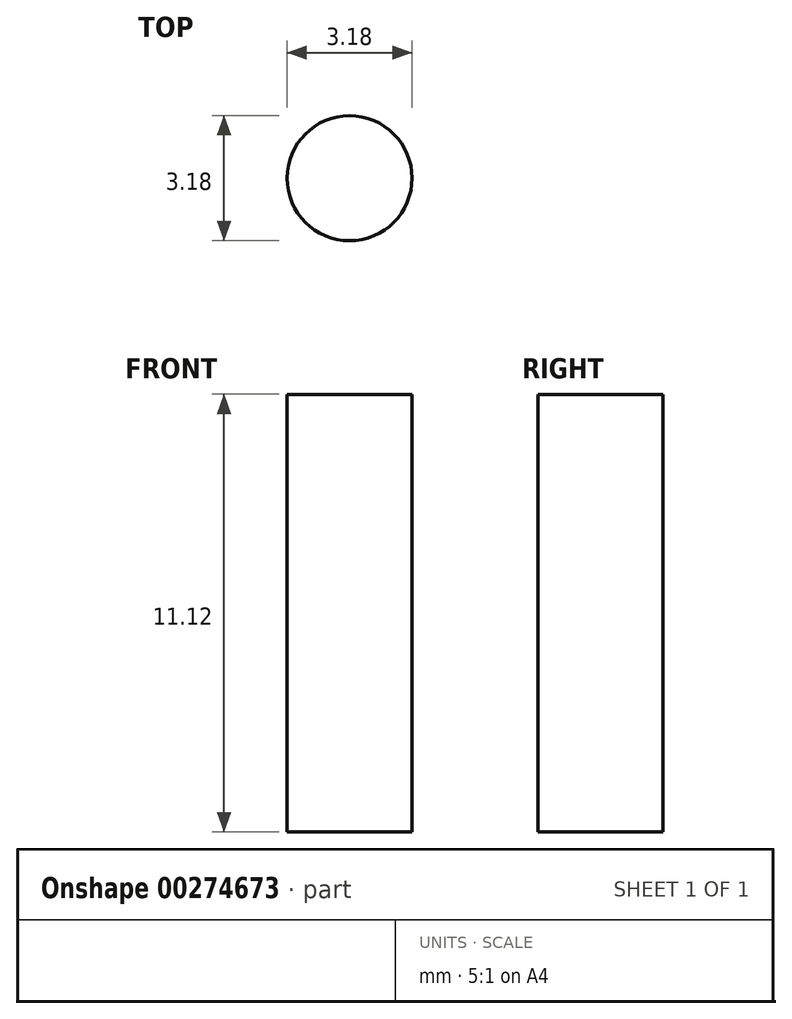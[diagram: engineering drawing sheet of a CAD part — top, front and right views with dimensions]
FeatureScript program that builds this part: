
annotation { "Feature Type Name" : "Feature", "Feature Type Description" : "" }
export const myFeature = defineFeature(function(context is Context, id is Id, definition is map)
    precondition{}
    {
        {
            var Q0;
            Q0=qCreatedBy(makeId("Top.planeOp"),FACE);
            var sketch = newSketch(context, id + "F0", { "sketchPlane" : qUnion([Q0])});
            skCircle(sketch, "E0", {"center": v(0, 0) * mm, "radius": 1.59 * mm});
            skSolve(sketch);
        }
        {
            var Q0;
            Q0 = qSketchRegion(id + "F0", true);
            extrude(context, id + "F1", {"entities" : qUnion([Q0]), "endBound" : BoundingType.SYMMETRIC, "depth" : 11.1 * mm});
        }
    });
